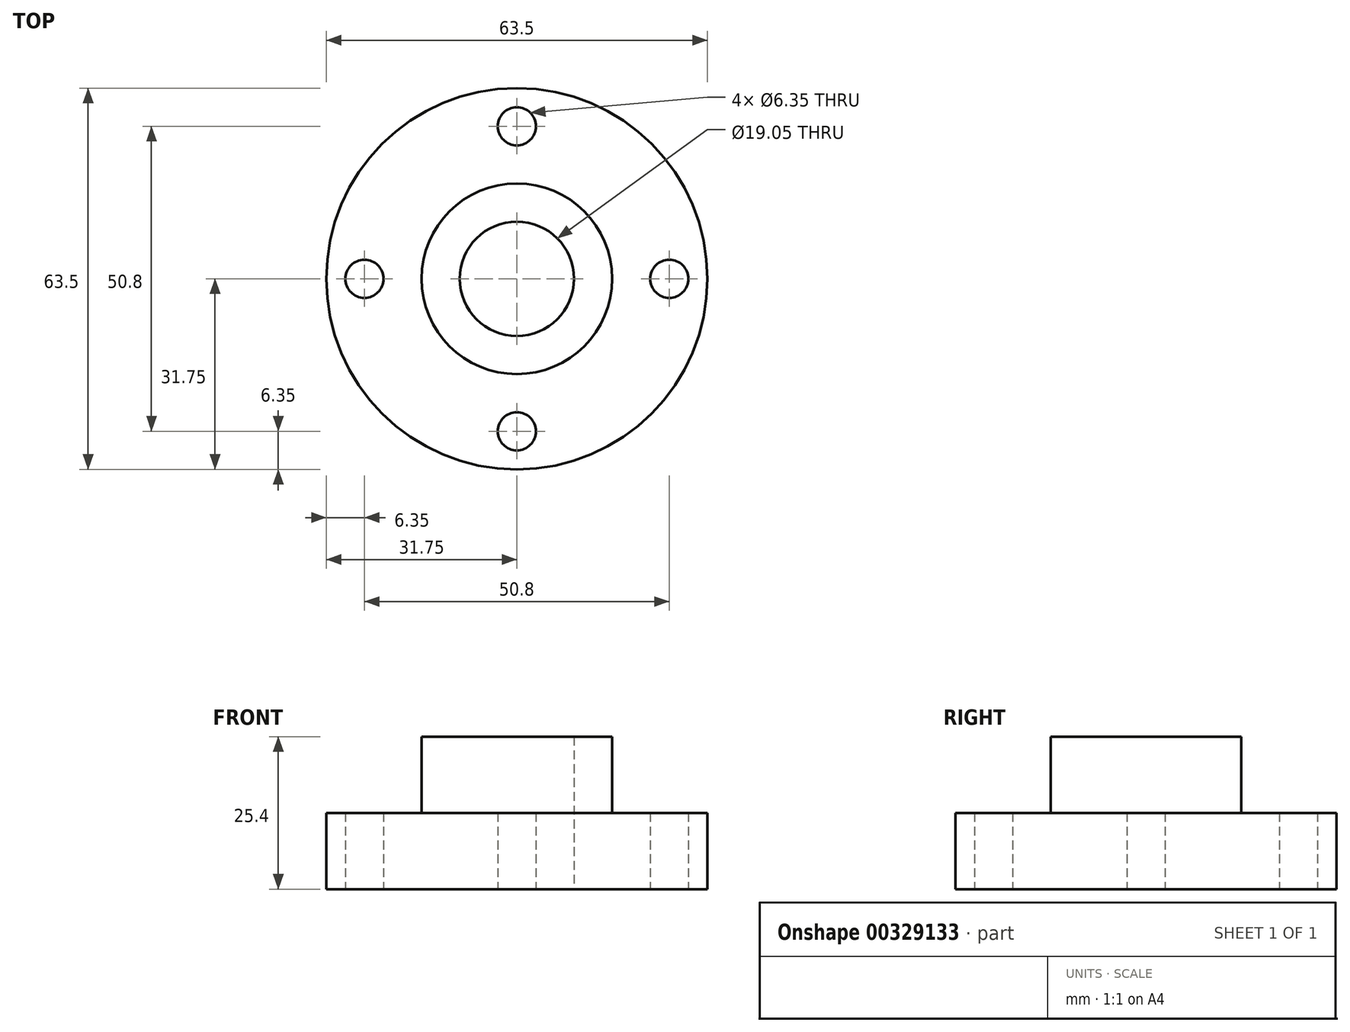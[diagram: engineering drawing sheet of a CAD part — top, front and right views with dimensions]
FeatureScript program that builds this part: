
annotation { "Feature Type Name" : "Feature", "Feature Type Description" : "" }
export const myFeature = defineFeature(function(context is Context, id is Id, definition is map)
    precondition{}
    {
        {
            var Q0;
            Q0=qCreatedBy(makeId("Top.planeOp"),FACE);
            var sketch = newSketch(context, id + "F0", { "sketchPlane" : qUnion([Q0])});
            skCircle(sketch, "E0", {"center": v(0, 0) * mm, "radius": 9.53 * mm});
            skCircle(sketch, "E1", {"center": v(0, 0) * mm, "radius": 15.88 * mm});
            skCircle(sketch, "E2", {"center": v(0, 0) * mm, "radius": 25.4 * mm});
            skCircle(sketch, "E3", {"center": v(0, 0) * mm, "radius": 31.75 * mm});
            skCircle(sketch, "E4", {"center": v(0, 25.4) * mm, "radius": 3.18 * mm});
            skCircle(sketch, "E5", {"center": v(-25.4, 0) * mm, "radius": 3.18 * mm});
            skCircle(sketch, "E6", {"center": v(0, -25.4) * mm, "radius": 3.18 * mm});
            skCircle(sketch, "E7", {"center": v(25.4, 0) * mm, "radius": 3.18 * mm});
            skSolve(sketch);
        }
        {
            var Q0;
            Q0=makeQuery(id+"F0.imprint","IMPRINT",FACE,{"disambiguationData":[TD([[makeQuery(id+"F0.imprint","IMPRINT",EDGE,{"derivedFrom":sQuery(id+"F0.wireOp",EDGE,"E1")}),-1.0]])]});
            var Q1;
            Q1=makeQuery(id+"F0.imprint","IMPRINT",FACE,{"disambiguationData":[TD([[makeQuery(id+"F0.imprint","IMPRINT",EDGE,{"derivedFrom":sQuery(id+"F0.wireOp",EDGE,"E3")}),1.0]])]});
            extrude(context, id + "F1", {"entities" : qUnion([Q0, Q1]), "depth" : 12.7 * mm});
        }
        {
            var Q0;
            Q0=makeQuery(id+"F0.imprint","IMPRINT",FACE,{"disambiguationData":[TD([[makeQuery(id+"F0.imprint","IMPRINT",EDGE,{"derivedFrom":sQuery(id+"F0.wireOp",EDGE,"E0")}),-1.0]])]});
            extrude(context, id + "F2", {"entities" : qUnion([Q0]), "operationType" : NewBodyOperationType.ADD, "depth" : 25.4 * mm});
        }
    });
